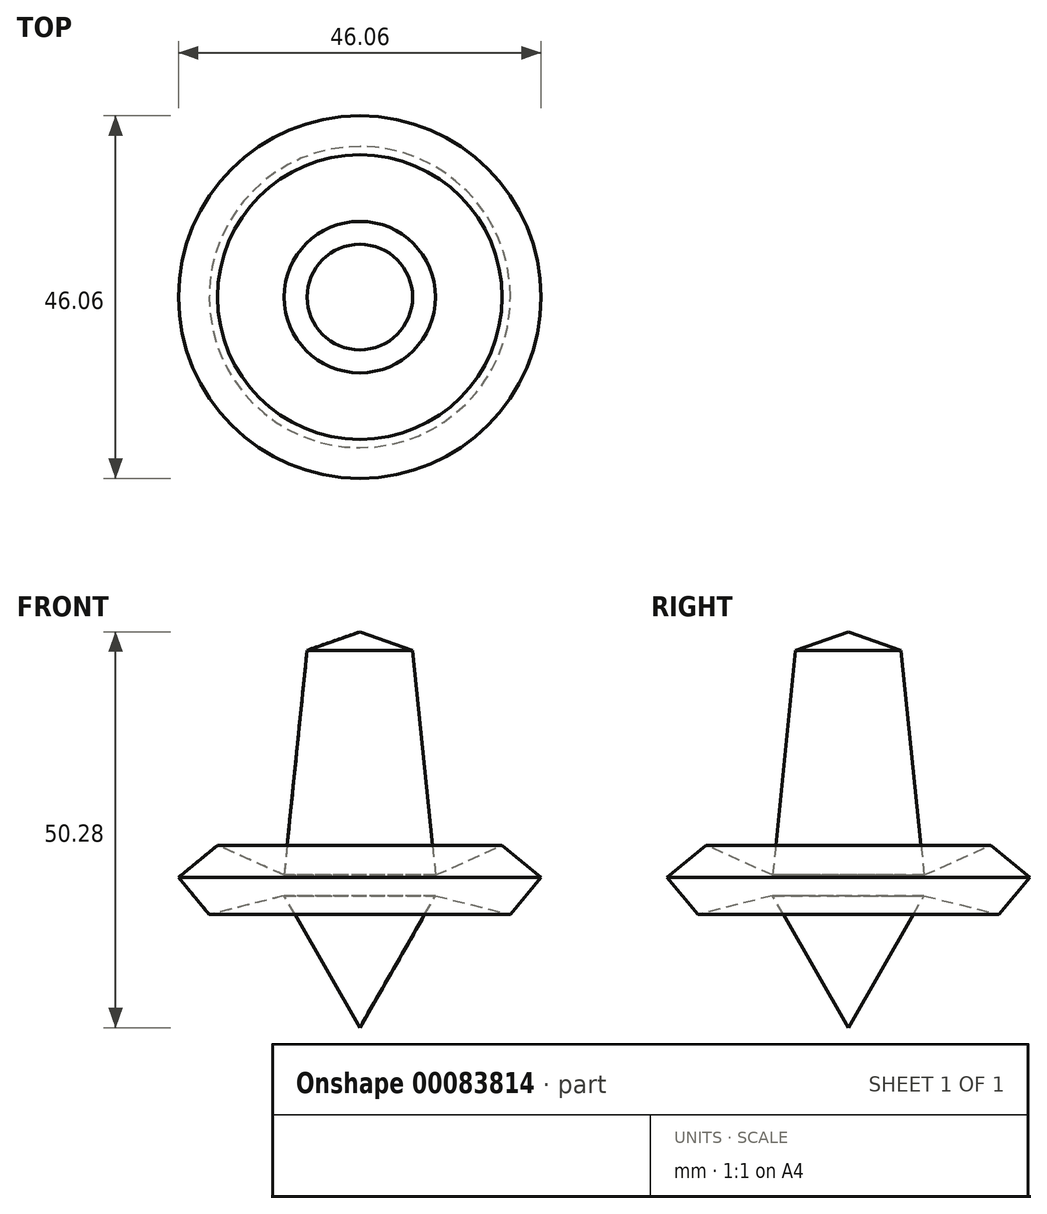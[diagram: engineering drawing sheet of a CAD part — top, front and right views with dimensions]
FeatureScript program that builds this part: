
annotation { "Feature Type Name" : "Feature", "Feature Type Description" : "" }
export const myFeature = defineFeature(function(context is Context, id is Id, definition is map)
    precondition{}
    {
        {
            var Q0;
            Q0=qCreatedBy(makeId("Front.planeOp"),FACE);
            var sketch = newSketch(context, id + "F0", { "sketchPlane" : qUnion([Q0])});
            skLineSegment(sketch, "E0", {"start": v(0, 0) * mm, "end": v(0, 50.28) * mm});
            skLineSegment(sketch, "E1", {"start": v(0, 50.28) * mm, "end": v(6.7, 47.95) * mm});
            skLineSegment(sketch, "E2", {"start": v(6.7, 47.95) * mm, "end": v(9.62, 19.38) * mm});
            skLineSegment(sketch, "E3", {"start": v(9.62, 19.38) * mm, "end": v(18.07, 23.17) * mm});
            skLineSegment(sketch, "E4", {"start": v(18.07, 23.17) * mm, "end": v(23.03, 19.1) * mm});
            skLineSegment(sketch, "E5", {"start": v(23.03, 19.1) * mm, "end": v(19.13, 14.36) * mm});
            skLineSegment(sketch, "E6", {"start": v(19.13, 14.36) * mm, "end": v(9.62, 16.76) * mm});
            skLineSegment(sketch, "E7", {"start": v(9.62, 16.76) * mm, "end": v(0, 0) * mm});
            skSolve(sketch);
        }
        {
            var Q0;
            Q0=makeQuery(id+"F0.imprint","IMPRINT",FACE,{"disambiguationData":[TD([[makeQuery(id+"F0.imprint","IMPRINT",EDGE,{"derivedFrom":sQuery(id+"F0.wireOp",EDGE,"E0")}),-1.0]])]});
            var Q1;
            Q1=sQuery(id+"F0.wireOp",EDGE,"E0");
            revolve(context, id + "F1", {"entities" : qUnion([Q0]), "axis" : qUnion([Q1]), "revolveType" : RevolveType.FULL});
        }
        {
            var Q0;
            Q0=qCreatedBy(makeId("Top.planeOp"),FACE);
            cPlane(context, id + "F2", {"entities" : qUnion([Q0]), "cplaneType" : CPlaneType.OFFSET, "offset" : 19.05 * mm, "width" : 152.4 * mm, "height" : 152.4 * mm});
        }
        {
            var Q0;
            Q0=qCreatedBy(id+"F2.planeOp",FACE);
            var sketch = newSketch(context, id + "F3", { "sketchPlane" : qUnion([Q0])});
            skLineSegment(sketch, "E8", {"start": v(0, 9.84) * mm, "end": v(0, 17.93) * mm});
            skLineSegment(sketch, "E9", {"start": v(6.62, 7.16) * mm, "end": v(12.41, 12.85) * mm});
            skLineSegment(sketch, "E10", {"start": v(0, 17.93) * mm, "end": v(2.76, 17.58) * mm});
            skLineSegment(sketch, "E11", {"start": v(3.7, 17.4) * mm, "end": v(5.7, 16.9) * mm});
            skLineSegment(sketch, "E12", {"start": v(7.75, 16.04) * mm, "end": v(9.8, 14.8) * mm});
            skLineSegment(sketch, "E13", {"start": v(10.53, 14.3) * mm, "end": v(12.41, 12.85) * mm});
            skPoint(sketch, "E14.visualSharp", {"position": v(3.23, 17.52) * mm});
            skArc(sketch, "E14.filletArc", {"start": v(3.7, 17.4) * mm, "mid": v(3.23, 17.5) * mm, "end": v(2.76, 17.58) * mm});
            skPoint(sketch, "E15.visualSharp", {"position": v(6.79, 16.61) * mm});
            skArc(sketch, "E15.filletArc", {"start": v(7.75, 16.04) * mm, "mid": v(6.75, 16.54) * mm, "end": v(5.7, 16.9) * mm});
            skPoint(sketch, "E16.visualSharp", {"position": v(10.18, 14.57) * mm});
            skArc(sketch, "E16.filletArc", {"start": v(10.53, 14.3) * mm, "mid": v(10.17, 14.56) * mm, "end": v(9.8, 14.8) * mm});
            skLineSegment(sketch, "E17", {"start": v(0, 9.84) * mm, "end": v(0.8, 9.84) * mm});
            skLineSegment(sketch, "E18", {"start": v(3.18, 9.38) * mm, "end": v(4.1, 9) * mm});
            skLineSegment(sketch, "E19", {"start": v(6.58, 7.21) * mm, "end": v(6.62, 7.16) * mm});
            skPoint(sketch, "E20.visualSharp", {"position": v(2.04, 9.84) * mm});
            skArc(sketch, "E20.filletArc", {"start": v(3.18, 9.38) * mm, "mid": v(2.01, 9.72) * mm, "end": v(0.8, 9.84) * mm});
            skPoint(sketch, "E21.visualSharp", {"position": v(5.56, 8.41) * mm});
            skArc(sketch, "E21.filletArc", {"start": v(6.58, 7.21) * mm, "mid": v(5.45, 8.26) * mm, "end": v(4.1, 9) * mm});
            skLineSegment(sketch, "E22.1.0", {"start": v(-9.36, 3.04) * mm, "end": v(-17.05, 5.54) * mm});
            skLineSegment(sketch, "E22.1.1", {"start": v(-17.05, 5.54) * mm, "end": v(-15.87, 8.05) * mm});
            skLineSegment(sketch, "E22.1.2", {"start": v(-15.4, 8.9) * mm, "end": v(-14.3, 10.64) * mm});
            skLineSegment(sketch, "E22.1.3", {"start": v(-4.76, 8.5) * mm, "end": v(-8.38, 15.77) * mm});
            skLineSegment(sketch, "E22.1.4", {"start": v(-10.35, 14.43) * mm, "end": v(-8.38, 15.77) * mm});
            skLineSegment(sketch, "E22.1.5", {"start": v(-12.86, 12.32) * mm, "end": v(-11.04, 13.9) * mm});
            skPoint(sketch, "E22.1.6", {"position": v(-13.7, 11.59) * mm});
            skArc(sketch, "E22.1.7", {"start": v(-12.86, 12.32) * mm, "mid": v(-13.64, 11.53) * mm, "end": v(-14.3, 10.64) * mm});
            skPoint(sketch, "E22.1.8", {"position": v(-15.67, 8.49) * mm});
            skPoint(sketch, "E22.1.9", {"position": v(-10.7, 14.18) * mm});
            skPoint(sketch, "E22.1.10", {"position": v(-6.28, 7.89) * mm});
            skArc(sketch, "E22.1.11", {"start": v(-7.93, 5.92) * mm, "mid": v(-8.62, 4.92) * mm, "end": v(-9.1, 3.8) * mm});
            skLineSegment(sketch, "E22.1.12", {"start": v(-7.93, 5.92) * mm, "end": v(-7.3, 6.68) * mm});
            skArc(sketch, "E22.1.13", {"start": v(-4.83, 8.48) * mm, "mid": v(-6.17, 7.73) * mm, "end": v(-7.3, 6.68) * mm});
            skLineSegment(sketch, "E22.2.0", {"start": v(-5.78, -7.96) * mm, "end": v(-10.54, -14.5) * mm});
            skLineSegment(sketch, "E22.2.1", {"start": v(-10.54, -14.5) * mm, "end": v(-12.56, -12.6) * mm});
            skLineSegment(sketch, "E22.2.2", {"start": v(-13.22, -11.9) * mm, "end": v(-14.54, -10.31) * mm});
            skLineSegment(sketch, "E22.2.3", {"start": v(-9.56, -1.9) * mm, "end": v(-17.6, -3.1) * mm});
            skLineSegment(sketch, "E22.2.4", {"start": v(-16.92, -5.38) * mm, "end": v(-17.6, -3.1) * mm});
            skLineSegment(sketch, "E22.2.5", {"start": v(-15.7, -8.42) * mm, "end": v(-16.63, -6.2) * mm});
            skPoint(sketch, "E22.2.6", {"position": v(-15.26, -9.45) * mm});
            skArc(sketch, "E22.2.7", {"start": v(-15.7, -8.42) * mm, "mid": v(-15.19, -9.4) * mm, "end": v(-14.54, -10.31) * mm});
            skPoint(sketch, "E22.2.8", {"position": v(-12.91, -12.28) * mm});
            skPoint(sketch, "E22.2.9", {"position": v(-16.8, -5.8) * mm});
            skPoint(sketch, "E22.2.10", {"position": v(-9.44, -3.54) * mm});
            skArc(sketch, "E22.2.11", {"start": v(-8.08, -5.72) * mm, "mid": v(-7.34, -6.68) * mm, "end": v(-6.43, -7.49) * mm});
            skLineSegment(sketch, "E22.2.12", {"start": v(-8.08, -5.72) * mm, "end": v(-8.6, -4.87) * mm});
            skArc(sketch, "E22.2.13", {"start": v(-9.56, -1.97) * mm, "mid": v(-9.26, -3.48) * mm, "end": v(-8.6, -4.87) * mm});
            skLineSegment(sketch, "E22.3.0", {"start": v(5.78, -7.96) * mm, "end": v(10.54, -14.5) * mm});
            skLineSegment(sketch, "E22.3.1", {"start": v(10.54, -14.5) * mm, "end": v(8.1, -15.84) * mm});
            skLineSegment(sketch, "E22.3.2", {"start": v(7.24, -16.25) * mm, "end": v(5.31, -17.02) * mm});
            skLineSegment(sketch, "E22.3.3", {"start": v(-1.15, -9.68) * mm, "end": v(-2.5, -17.69) * mm});
            skLineSegment(sketch, "E22.3.4", {"start": v(-0.11, -17.76) * mm, "end": v(-2.5, -17.69) * mm});
            skLineSegment(sketch, "E22.3.5", {"start": v(3.16, -17.53) * mm, "end": v(0.77, -17.73) * mm});
            skPoint(sketch, "E22.3.6", {"position": v(4.27, -17.43) * mm});
            skArc(sketch, "E22.3.7", {"start": v(3.16, -17.53) * mm, "mid": v(4.26, -17.35) * mm, "end": v(5.31, -17.02) * mm});
            skPoint(sketch, "E22.3.8", {"position": v(7.68, -16.07) * mm});
            skPoint(sketch, "E22.3.9", {"position": v(0.33, -17.77) * mm});
            skPoint(sketch, "E22.3.10", {"position": v(0.45, -10.08) * mm});
            skArc(sketch, "E22.3.11", {"start": v(2.94, -9.45) * mm, "mid": v(4.08, -9.05) * mm, "end": v(5.13, -8.43) * mm});
            skLineSegment(sketch, "E22.3.12", {"start": v(2.94, -9.45) * mm, "end": v(1.98, -9.7) * mm});
            skArc(sketch, "E22.3.13", {"start": v(-1.08, -9.7) * mm, "mid": v(0.45, -9.88) * mm, "end": v(1.98, -9.7) * mm});
            skLineSegment(sketch, "E22.4.0", {"start": v(9.36, 3.04) * mm, "end": v(17.05, 5.54) * mm});
            skLineSegment(sketch, "E22.4.1", {"start": v(17.05, 5.54) * mm, "end": v(17.57, 2.81) * mm});
            skLineSegment(sketch, "E22.4.2", {"start": v(17.7, 1.86) * mm, "end": v(17.83, -0.2) * mm});
            skLineSegment(sketch, "E22.4.3", {"start": v(8.85, -4.09) * mm, "end": v(16.05, -7.83) * mm});
            skLineSegment(sketch, "E22.4.4", {"start": v(16.85, -5.6) * mm, "end": v(16.05, -7.83) * mm});
            skLineSegment(sketch, "E22.4.5", {"start": v(17.64, -2.41) * mm, "end": v(17.1, -4.75) * mm});
            skPoint(sketch, "E22.4.6", {"position": v(17.9, -1.32) * mm});
            skArc(sketch, "E22.4.7", {"start": v(17.64, -2.41) * mm, "mid": v(17.82, -1.31) * mm, "end": v(17.83, -0.2) * mm});
            skPoint(sketch, "E22.4.8", {"position": v(17.66, 2.34) * mm});
            skPoint(sketch, "E22.4.9", {"position": v(17, -5.18) * mm});
            skPoint(sketch, "E22.4.10", {"position": v(9.72, -2.69) * mm});
            skArc(sketch, "E22.4.11", {"start": v(9.9, -0.13) * mm, "mid": v(9.87, 1.09) * mm, "end": v(9.6, 2.28) * mm});
            skLineSegment(sketch, "E22.4.12", {"start": v(9.9, -0.13) * mm, "end": v(9.83, -1.12) * mm});
            skArc(sketch, "E22.4.13", {"start": v(8.9, -4.03) * mm, "mid": v(9.54, -2.63) * mm, "end": v(9.83, -1.12) * mm});
            skPoint(sketch, "E22.center", {"position": v(0, 0) * mm});
            skSolve(sketch);
        }
        {
            var Q0;
            Q0=makeQuery(id+"F1.opRevolve","SWEPT_BODY",BODY,{"disambiguationData":[OSD([sQuery(id+"F0.wireOp",EDGE,"E0"),sQuery(id+"F0.wireOp",EDGE,"E1"),sQuery(id+"F0.wireOp",EDGE,"E2"),sQuery(id+"F0.wireOp",EDGE,"E3"),sQuery(id+"F0.wireOp",EDGE,"E4"),sQuery(id+"F0.wireOp",EDGE,"E5"),sQuery(id+"F0.wireOp",EDGE,"E6"),sQuery(id+"F0.wireOp",EDGE,"E7")])]});
            var Q1;
            Q1=makeQuery(id+"F1.opRevolve","SWEPT_FACE",FACE,{"disambiguationData":[OSD([sQuery(id+"F0.wireOp",EDGE,"E1")])]});
            circularPattern(context, id + "F4", {"entities" : qUnion([Q0]), "axis" : qUnion([Q1]), "angle" : 72 * degree, "instanceCount" : 5});
        }
    });
